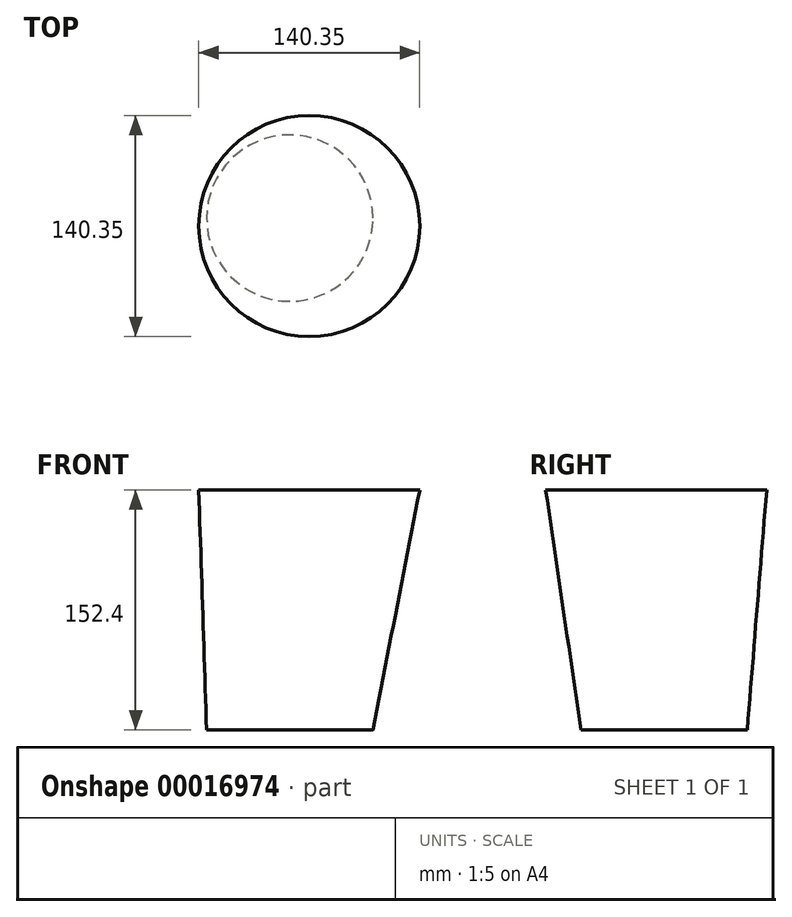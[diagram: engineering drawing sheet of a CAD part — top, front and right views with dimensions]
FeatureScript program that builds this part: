
annotation { "Feature Type Name" : "Feature", "Feature Type Description" : "" }
export const myFeature = defineFeature(function(context is Context, id is Id, definition is map)
    precondition{}
    {
        {
            var Q0;
            Q0=qCreatedBy(makeId("Top.planeOp"),FACE);
            cPlane(context, id + "F0", {"entities" : qUnion([Q0]), "cplaneType" : CPlaneType.OFFSET, "offset" : 152.4 * mm, "width" : 152.4 * mm, "height" : 152.4 * mm});
        }
        {
            var Q0;
            Q0=qCreatedBy(id+"F0.planeOp",FACE);
            var sketch = newSketch(context, id + "F1", { "sketchPlane" : qUnion([Q0])});
            skCircle(sketch, "E0", {"center": v(12.36, -5.06) * mm, "radius": 70.18 * mm});
            skSolve(sketch);
        }
        {
            var Q0;
            Q0=qCreatedBy(makeId("Top.planeOp"),FACE);
            var sketch = newSketch(context, id + "F2", { "sketchPlane" : qUnion([Q0])});
            skCircle(sketch, "E1", {"center": v(0, 0) * mm, "radius": 52.83 * mm});
            skSolve(sketch);
        }
        {
            var Q0;
            Q0=makeQuery(id+"F1.imprint","IMPRINT",FACE,{"disambiguationData":[TD([[makeQuery(id+"F1.imprint","IMPRINT",EDGE,{"derivedFrom":sQuery(id+"F1.wireOp",EDGE,"E0")}),1.0]])]});
            var Q1;
            Q1=makeQuery(id+"F2.imprint","IMPRINT",FACE,{"disambiguationData":[TD([[makeQuery(id+"F2.imprint","IMPRINT",EDGE,{"derivedFrom":sQuery(id+"F2.wireOp",EDGE,"E1")}),1.0]])]});
            loft(context, id + "F3", {"sheetProfilesArray" : [{ "sheetProfileEntities" : qUnion([Q0]) }, { "sheetProfileEntities" : qUnion([Q1]) }]});
        }
    });
